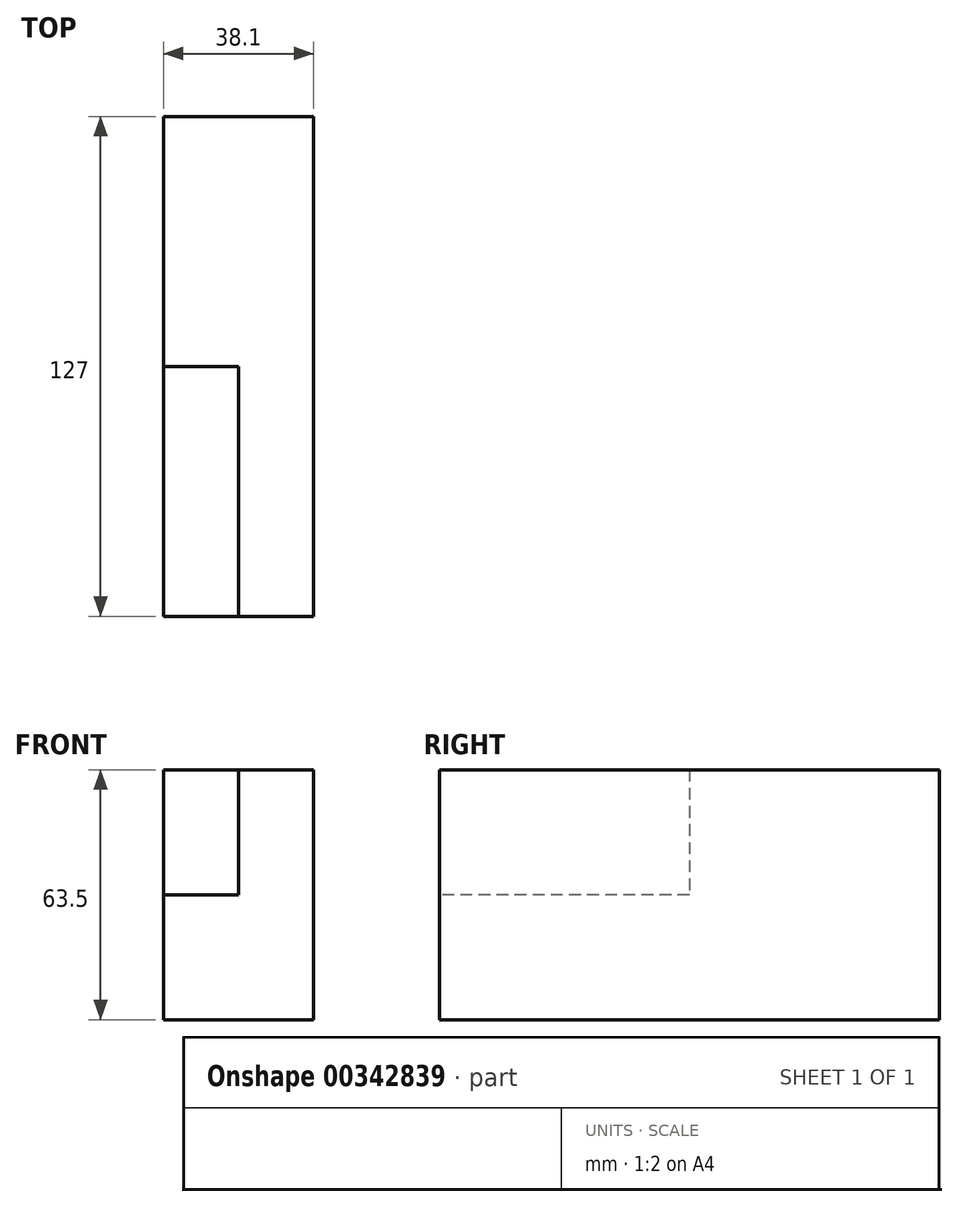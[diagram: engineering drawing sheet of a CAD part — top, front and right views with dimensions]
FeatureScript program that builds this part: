
annotation { "Feature Type Name" : "Feature", "Feature Type Description" : "" }
export const myFeature = defineFeature(function(context is Context, id is Id, definition is map)
    precondition{}
    {
        {
            var Q0;
            Q0=qCreatedBy(makeId("Top.planeOp"),FACE);
            var sketch = newSketch(context, id + "F0", { "sketchPlane" : qUnion([Q0])});
            skLineSegment(sketch, "E0.bottom", {"start": v(0, 76.76) * mm, "end": v(38.1, 76.76) * mm});
            skLineSegment(sketch, "E0.top", {"start": v(19.05, -50.24) * mm, "end": v(38.1, -50.24) * mm});
            skLineSegment(sketch, "E0.left", {"start": v(0, 76.76) * mm, "end": v(0, 13.26) * mm});
            skLineSegment(sketch, "E0.right", {"start": v(38.1, 76.76) * mm, "end": v(38.1, -50.24) * mm});
            skLineSegment(sketch, "E1", {"start": v(19.05, -50.24) * mm, "end": v(19.05, 13.26) * mm});
            skLineSegment(sketch, "E2", {"start": v(19.05, 13.26) * mm, "end": v(0, 13.26) * mm});
            skPoint(sketch, "E3.orphan", {"position": v(0, -50.24) * mm});
            skLineSegment(sketch, "E4", {"start": v(0, 13.26) * mm, "end": v(0, -50.24) * mm});
            skLineSegment(sketch, "E5", {"start": v(0, -50.24) * mm, "end": v(19.05, -50.24) * mm});
            skSolve(sketch);
        }
        {
            var Q0;
            Q0=makeQuery(id+"F0.imprint","IMPRINT",FACE,{"disambiguationData":[TD([[makeQuery(id+"F0.imprint","IMPRINT",EDGE,{"derivedFrom":sQuery(id+"F0.wireOp",EDGE,"E0.bottom")}),-1.0]])]});
            extrude(context, id + "F1", {"entities" : qUnion([Q0]), "depth" : 63.5 * mm});
        }
        {
            var Q0;
            Q0 = qSketchRegion(id + "F0", true);
            extrude(context, id + "F2", {"entities" : qUnion([Q0]), "operationType" : NewBodyOperationType.ADD, "depth" : 31.75 * mm});
        }
    });
